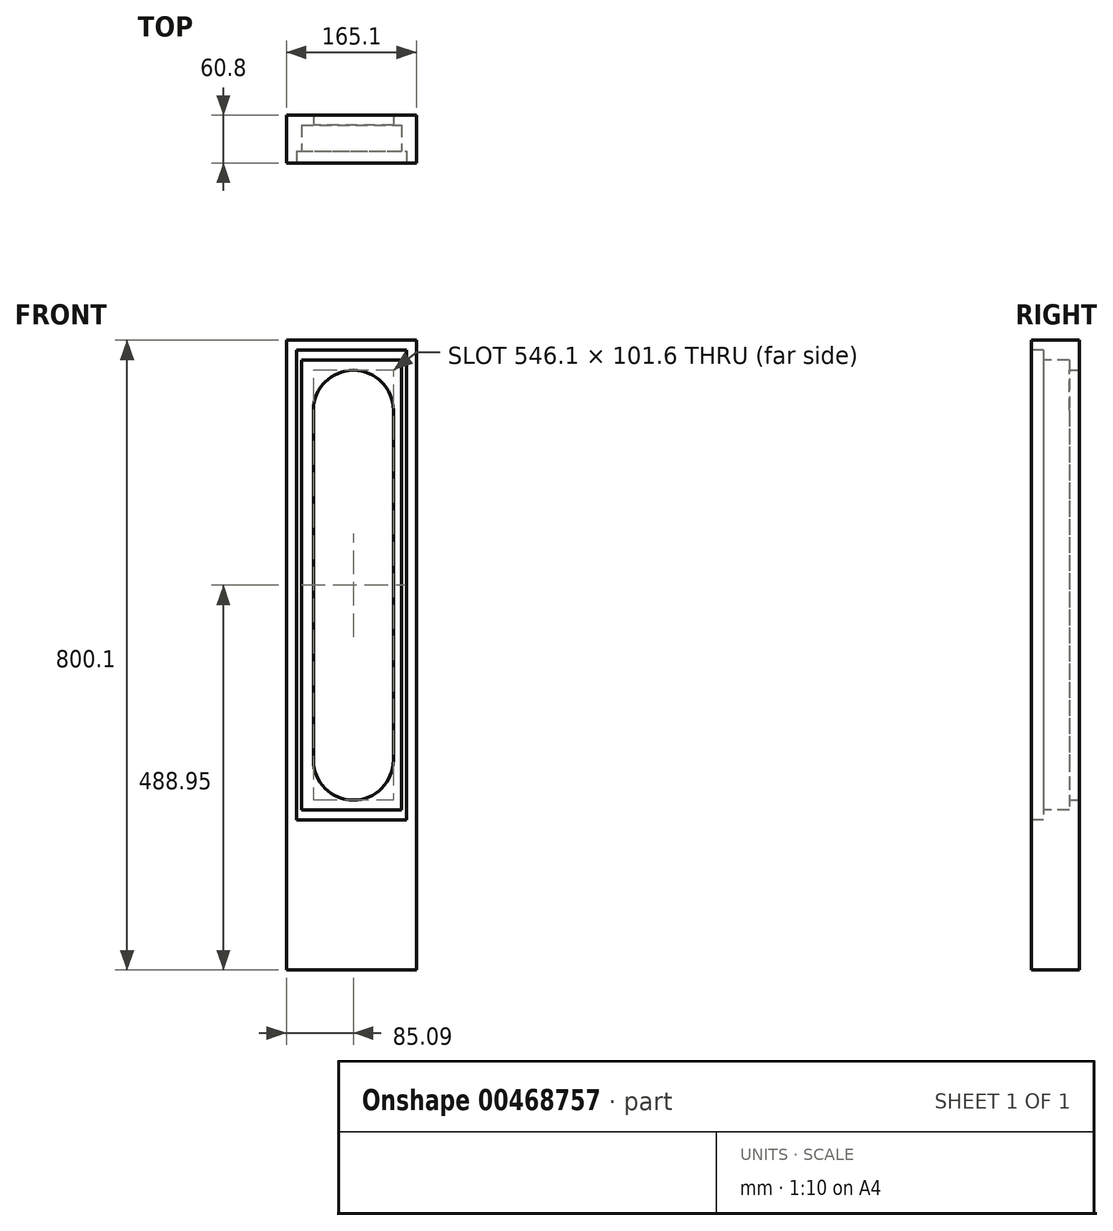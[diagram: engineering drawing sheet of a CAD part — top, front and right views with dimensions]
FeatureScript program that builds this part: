
annotation { "Feature Type Name" : "Feature", "Feature Type Description" : "" }
export const myFeature = defineFeature(function(context is Context, id is Id, definition is map)
    precondition{}
    {
        {
            var Q0;
            Q0=qCreatedBy(makeId("Front.planeOp"),FACE);
            var sketch = newSketch(context, id + "F0", { "sketchPlane" : qUnion([Q0])});
            skLineSegment(sketch, "E0.top", {"start": v(82.55, 609.6) * mm, "end": v(-82.55, 609.6) * mm});
            skLineSegment(sketch, "E0.left", {"start": v(82.55, -190.5) * mm, "end": v(82.55, 609.6) * mm});
            skLineSegment(sketch, "E0.right", {"start": v(-82.55, -190.5) * mm, "end": v(-82.55, 609.6) * mm});
            skPoint(sketch, "E1.middle", {"position": v(0, 0) * mm});
            skLineSegment(sketch, "E2", {"start": v(-82.55, -190.5) * mm, "end": v(82.55, -190.5) * mm});
            skPoint(sketch, "E3.orphan", {"position": v(-82.55, -609.6) * mm});
            skPoint(sketch, "E4.orphan", {"position": v(82.55, -609.6) * mm});
            skLineSegment(sketch, "E5.bottom", {"start": v(-69.85, 596.9) * mm, "end": v(69.85, 596.9) * mm});
            skLineSegment(sketch, "E5.top", {"start": v(-69.85, 0) * mm, "end": v(69.85, 0) * mm});
            skLineSegment(sketch, "E5.left", {"start": v(-69.85, 596.9) * mm, "end": v(-69.85, 0) * mm});
            skLineSegment(sketch, "E5.right", {"start": v(69.85, 596.9) * mm, "end": v(69.85, 0) * mm});
            skLineSegment(sketch, "E6.bottom", {"start": v(-63.5, 584.2) * mm, "end": v(63.5, 584.2) * mm});
            skLineSegment(sketch, "E6.top", {"start": v(-63.5, 12.7) * mm, "end": v(63.5, 12.7) * mm});
            skLineSegment(sketch, "E6.left", {"start": v(-63.5, 584.2) * mm, "end": v(-63.5, 12.7) * mm});
            skLineSegment(sketch, "E6.right", {"start": v(63.5, 584.2) * mm, "end": v(63.5, 12.7) * mm});
            skLineSegment(sketch, "E7.bottom", {"start": v(-48.26, 571.5) * mm, "end": v(53.34, 571.5) * mm});
            skLineSegment(sketch, "E7.top", {"start": v(-48.26, 25.4) * mm, "end": v(53.34, 25.4) * mm});
            skLineSegment(sketch, "E7.left", {"start": v(-48.26, 571.5) * mm, "end": v(-48.26, 25.4) * mm});
            skLineSegment(sketch, "E7.right", {"start": v(53.34, 571.5) * mm, "end": v(53.34, 25.4) * mm});
            skLineSegment(sketch, "E8", {"start": v(0, 755.14) * mm, "end": v(0, -755.14) * mm, "construction": true});
            skSolve(sketch);
        }
        {
            var Q0;
            Q0=makeQuery(id+"F0.imprint","IMPRINT",FACE,{"disambiguationData":[TD([[makeQuery(id+"F0.imprint","IMPRINT",EDGE,{"derivedFrom":sQuery(id+"F0.wireOp",EDGE,"E0.top")}),1.0]])]});
            var Q1;
            Q1=makeQuery(id+"F0.imprint","IMPRINT",FACE,{"disambiguationData":[TD([[makeQuery(id+"F0.imprint","IMPRINT",EDGE,{"derivedFrom":sQuery(id+"F0.wireOp",EDGE,"E1.bottom")}),-1.0]])]});
            var Q2;
            Q2=makeQuery(id+"F0.imprint","IMPRINT",FACE,{"disambiguationData":[TD([[makeQuery(id+"F0.imprint","IMPRINT",EDGE,{"derivedFrom":sQuery(id+"F0.wireOp",EDGE,"l2cz76WN-11cX-8Qg5-Wc74-vKwfhGCtYGeO.bottom")}),-1.0]])]});
            var Q3;
            {var subQ0=sQuery(id+"F0.wireOp",EDGE,"dQK7Thth-TP6K-kbBQ-5Cwl-0GHNaYrmpQfn.left");var subQ1=sQuery(id+"F0.wireOp",EDGE,"E1.bottom");var subQ2=makeQuery(id+"F0.imprint","INTERSECT",VERTEX,{"derivedFrom":[subQ1,subQ0]});Q3=makeQuery(id+"F0.imprint","IMPRINT",FACE,{"disambiguationData":[TD([[makeQuery(id+"F0.imprint","IMPRINT",EDGE,{"disambiguationData":[TD([[subQ2,-1.0]])],"derivedFrom":subQ1}),1.0]])]});}
            var Q4;
            {var subQ5=sQuery(id+"F0.wireOp",EDGE,"huDVYpq4-8GHm-f6ov-cYvV-LWDsyoBmHsaB.top");Q4=makeQuery(id+"F0.imprint","IMPRINT",FACE,{"disambiguationData":[TD([[makeQuery(id+"F0.imprint","IMPRINT",EDGE,{"derivedFrom":subQ5}),1.0]])]});}
            var Q5;
            {var subQ5=sQuery(id+"F0.wireOp",EDGE,"dQK7Thth-TP6K-kbBQ-5Cwl-0GHNaYrmpQfn.bottom");Q5=makeQuery(id+"F0.imprint","IMPRINT",FACE,{"disambiguationData":[TD([[makeQuery(id+"F0.imprint","IMPRINT",EDGE,{"derivedFrom":subQ5}),-1.0]])]});}
            var Q6;
            {var subQ5=sQuery(id+"F0.wireOp",EDGE,"dQK7Thth-TP6K-kbBQ-5Cwl-0GHNaYrmpQfn.top");Q6=makeQuery(id+"F0.imprint","IMPRINT",FACE,{"disambiguationData":[TD([[makeQuery(id+"F0.imprint","IMPRINT",EDGE,{"derivedFrom":subQ5}),1.0]])]});}
            var Q7;
            {var subQ5=sQuery(id+"F0.wireOp",EDGE,"huDVYpq4-8GHm-f6ov-cYvV-LWDsyoBmHsaB.bottom");Q7=makeQuery(id+"F0.imprint","IMPRINT",FACE,{"disambiguationData":[TD([[makeQuery(id+"F0.imprint","IMPRINT",EDGE,{"derivedFrom":subQ5}),-1.0]])]});}
            var Q8;
            {var subQ0=sQuery(id+"F0.wireOp",EDGE,"dQK7Thth-TP6K-kbBQ-5Cwl-0GHNaYrmpQfn.left");var subQ1=sQuery(id+"F0.wireOp",EDGE,"E1.bottom");var subQ2=makeQuery(id+"F0.imprint","INTERSECT",VERTEX,{"derivedFrom":[subQ1,subQ0]});Q8=makeQuery(id+"F0.imprint","IMPRINT",FACE,{"disambiguationData":[TD([[makeQuery(id+"F0.imprint","IMPRINT",EDGE,{"disambiguationData":[TD([[subQ2,-1.0]])],"derivedFrom":subQ1}),-1.0]])]});}
            var Q9;
            Q9=makeQuery(id+"F0.imprint","IMPRINT",FACE,{"disambiguationData":[TD([[makeQuery(id+"F0.imprint","IMPRINT",EDGE,{"derivedFrom":sQuery(id+"F0.wireOp",EDGE,"E6.bottom")}),-1.0]])]});
            var Q10;
            Q10=makeQuery(id+"F0.imprint","IMPRINT",FACE,{"disambiguationData":[TD([[makeQuery(id+"F0.imprint","IMPRINT",EDGE,{"derivedFrom":sQuery(id+"F0.wireOp",EDGE,"E5.bottom")}),-1.0]])]});
            extrude(context, id + "F1", {"entities" : qUnion([Q0, Q1, Q2, Q3, Q4, Q5, Q6, Q7, Q8, Q9, Q10]), "oppositeDirection" : true, "depth" : 50.8 * mm});
        }
        {
            var Q0;
            Q0=makeQuery(id+"F0.imprint","IMPRINT",FACE,{"disambiguationData":[TD([[makeQuery(id+"F0.imprint","IMPRINT",EDGE,{"derivedFrom":sQuery(id+"F0.wireOp",EDGE,"E5.bottom")}),-1.0]])]});
            extrude(context, id + "F2", {"entities" : qUnion([Q0]), "operationType" : NewBodyOperationType.REMOVE, "oppositeDirection" : true, "depth" : 5 * mm});
        }
        {
            var Q0;
            Q0=makeQuery(id+"F0.imprint","IMPRINT",FACE,{"disambiguationData":[TD([[makeQuery(id+"F0.imprint","IMPRINT",EDGE,{"derivedFrom":sQuery(id+"F0.wireOp",EDGE,"E6.bottom")}),-1.0]])]});
            extrude(context, id + "F3", {"entities" : qUnion([Q0]), "operationType" : NewBodyOperationType.REMOVE, "oppositeDirection" : true, "depth" : 38.1 * mm});
        }
        {
            var Q0;
            Q0=makeQuery(id+"F1.opExtrude","SWEPT_EDGE",EDGE,{"disambiguationData":[OSD([sQuery(id+"F0.wireOp",EDGE,"E7.bottom"),sQuery(id+"F0.wireOp",EDGE,"E7.right")])]});
            var Q1;
            Q1=makeQuery(id+"F1.opExtrude","SWEPT_EDGE",EDGE,{"disambiguationData":[OSD([sQuery(id+"F0.wireOp",EDGE,"E7.bottom"),sQuery(id+"F0.wireOp",EDGE,"E7.left")])]});
            var Q2;
            Q2=makeQuery(id+"F1.opExtrude","SWEPT_EDGE",EDGE,{"disambiguationData":[OSD([sQuery(id+"F0.wireOp",EDGE,"E7.top"),sQuery(id+"F0.wireOp",EDGE,"E7.left")])]});
            var Q3;
            Q3=makeQuery(id+"F1.opExtrude","SWEPT_EDGE",EDGE,{"disambiguationData":[OSD([sQuery(id+"F0.wireOp",EDGE,"E7.top"),sQuery(id+"F0.wireOp",EDGE,"E7.right")])]});
            fillet(context, id + "F4", {"entities" : qUnion([Q0, Q1, Q2, Q3]), "radius" : 50.8 * mm, "tangentPropagation" : true, "allowEdgeOverflow" : false});
        }
        {
            var Q0;
            Q0 = qSketchRegion(id + "F0", true);
            var Q1;
            {var subQ0=sQuery(id+"F0.wireOp",EDGE,"E0.right");var subQ1=sQuery(id+"F0.wireOp",EDGE,"E0.left");var subQ2=sQuery(id+"F0.wireOp",EDGE,"E2");var subQ3=sQuery(id+"F0.wireOp",EDGE,"E0.top");Q1=makeQuery(id+"F2.boolean.opBoolean","SPLIT",FACE,{"disambiguationData":[TD([makeQuery(id+"F1.opExtrude","SWEPT_FACE",FACE,{"disambiguationData":[OSD([subQ3])]})])],"derivedFrom":makeQuery(id+"F1.opExtrude","CAP_FACE",FACE,{"disambiguationData":[OSD([subQ3,subQ1,subQ0,subQ2,sQuery(id+"F0.wireOp",EDGE,"E7.bottom"),sQuery(id+"F0.wireOp",EDGE,"E7.top"),sQuery(id+"F0.wireOp",EDGE,"E7.left"),sQuery(id+"F0.wireOp",EDGE,"E7.right")])],"isStart":true})});}
            extrude(context, id + "F5", {"entities" : qUnion([Q0, Q1]), "operationType" : NewBodyOperationType.ADD, "depth" : 10 * mm});
        }
    });
